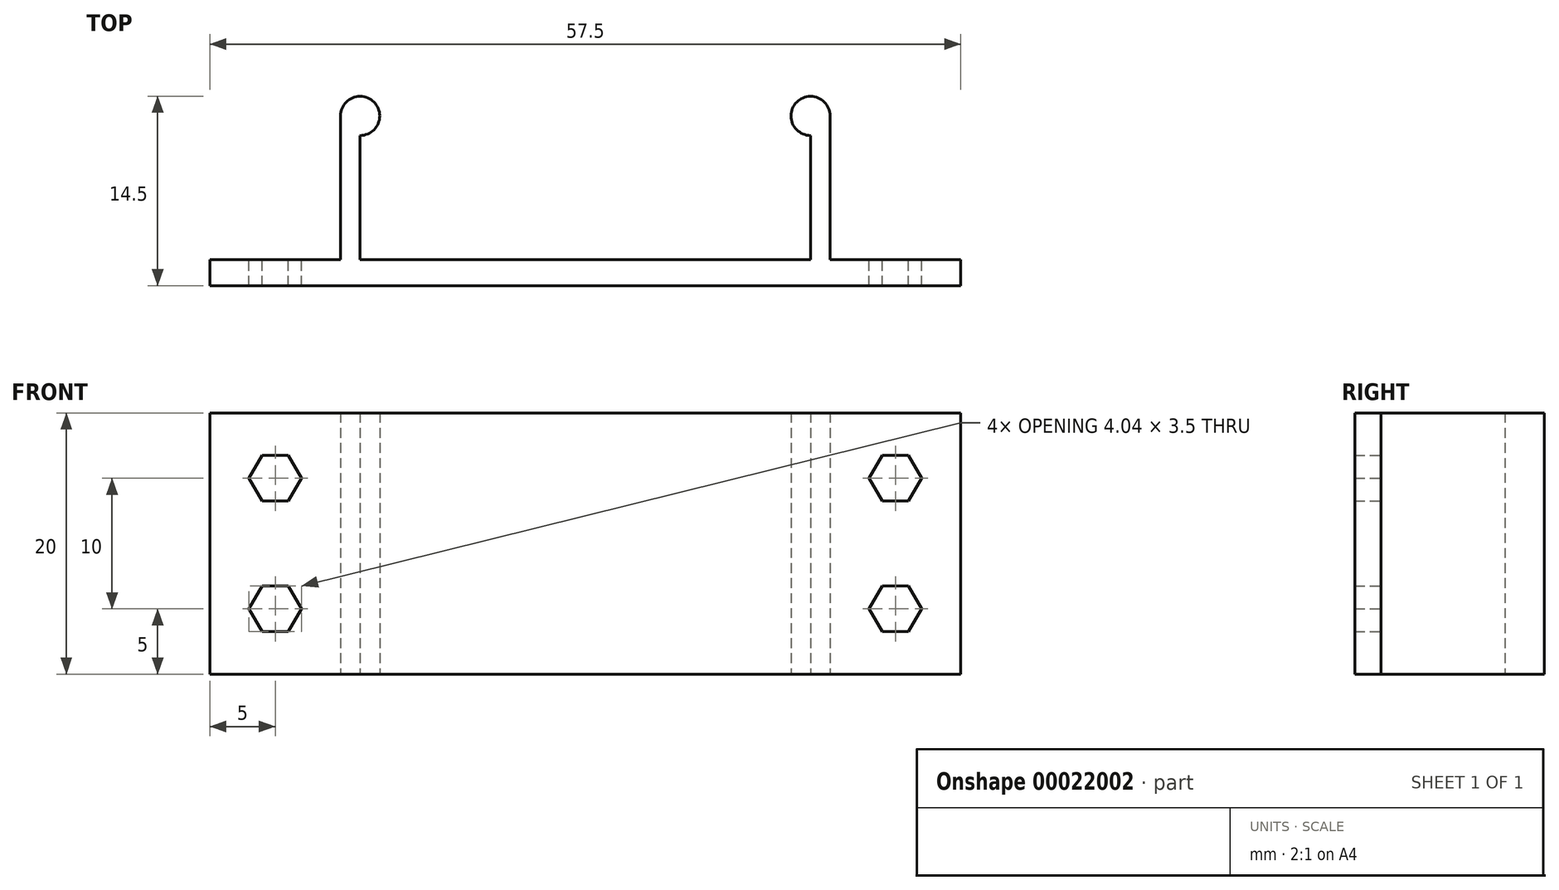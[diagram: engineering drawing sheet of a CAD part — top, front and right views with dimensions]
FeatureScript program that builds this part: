
annotation { "Feature Type Name" : "Feature", "Feature Type Description" : "" }
export const myFeature = defineFeature(function(context is Context, id is Id, definition is map)
    precondition{}
    {
        {
            var Q0;
            Q0=qCreatedBy(makeId("Top.planeOp"),FACE);
            var sketch = newSketch(context, id + "F0", { "sketchPlane" : qUnion([Q0])});
            skLineSegment(sketch, "E0.rect.bottom", {"start": v(17.25, -5.5) * mm, "end": v(-17.25, -5.5) * mm, "construction": true});
            skLineSegment(sketch, "E0.rect.top", {"start": v(17.25, 5.5) * mm, "end": v(-17.25, 5.5) * mm, "construction": true});
            skLineSegment(sketch, "E0.rect.left", {"start": v(17.25, -5.5) * mm, "end": v(17.25, 5.5) * mm, "construction": true});
            skLineSegment(sketch, "E0.rect.right", {"start": v(-17.25, -5.5) * mm, "end": v(-17.25, 5.5) * mm, "construction": true});
            skPoint(sketch, "E0.rect.middle", {"position": v(0, 0) * mm});
            skLineSegment(sketch, "E1", {"start": v(-17.25, 4) * mm, "end": v(-17.25, -5.5) * mm});
            skLineSegment(sketch, "E2", {"start": v(-17.25, -5.5) * mm, "end": v(17.25, -5.5) * mm});
            skLineSegment(sketch, "E3", {"start": v(17.25, -5.5) * mm, "end": v(17.25, 4) * mm});
            skLineSegment(sketch, "E4", {"start": v(-17.25, 5.5) * mm, "end": v(-18.75, 5.5) * mm, "construction": true});
            skLineSegment(sketch, "E5", {"start": v(-18.75, 5.5) * mm, "end": v(-18.75, -5.5) * mm});
            skLineSegment(sketch, "E6", {"start": v(-18.75, -5.5) * mm, "end": v(-28.75, -5.5) * mm});
            skLineSegment(sketch, "E7", {"start": v(-28.75, -5.5) * mm, "end": v(-28.75, -7.5) * mm});
            skLineSegment(sketch, "E8", {"start": v(-28.75, -7.5) * mm, "end": v(28.75, -7.5) * mm});
            skLineSegment(sketch, "E9", {"start": v(28.75, -7.5) * mm, "end": v(28.75, -5.5) * mm});
            skLineSegment(sketch, "E10", {"start": v(28.75, -5.5) * mm, "end": v(18.75, -5.5) * mm});
            skLineSegment(sketch, "E11", {"start": v(18.75, -5.5) * mm, "end": v(18.75, 5.5) * mm});
            skLineSegment(sketch, "E12", {"start": v(18.75, 5.5) * mm, "end": v(17.25, 5.5) * mm, "construction": true});
            skArc(sketch, "E13", {"start": v(-17.25, 4) * mm, "mid": v(-16.19, 6.56) * mm, "end": v(-18.75, 5.5) * mm});
            skArc(sketch, "E14", {"start": v(18.75, 5.5) * mm, "mid": v(16.19, 6.56) * mm, "end": v(17.25, 4) * mm});
            skSolve(sketch);
        }
        {
            var Q0;
            Q0 = qSketchRegion(id + "F0", true);
            extrude(context, id + "F1", {"entities" : qUnion([Q0]), "depth" : 20 * mm});
        }
        {
            var Q0;
            Q0=qCreatedBy(makeId("Front.planeOp"),FACE);
            var sketch = newSketch(context, id + "F2", { "sketchPlane" : qUnion([Q0])});
            skCircle(sketch, "E15.cCircle", {"center": v(23.75, 15) * mm, "radius": 1.75 * mm, "construction": true});
            skLineSegment(sketch, "E15.0", {"start": v(22.74, 13.25) * mm, "end": v(21.73, 15) * mm});
            skLineSegment(sketch, "E15.1", {"start": v(21.73, 15) * mm, "end": v(22.74, 16.75) * mm});
            skLineSegment(sketch, "E15.2", {"start": v(22.74, 16.75) * mm, "end": v(24.76, 16.75) * mm});
            skLineSegment(sketch, "E15.3", {"start": v(24.76, 16.75) * mm, "end": v(25.77, 15) * mm});
            skLineSegment(sketch, "E15.4", {"start": v(25.77, 15) * mm, "end": v(24.76, 13.25) * mm});
            skLineSegment(sketch, "E15.5", {"start": v(24.76, 13.25) * mm, "end": v(22.74, 13.25) * mm});
            skPoint(sketch, "E15.0.midPoint", {"position": v(22.23, 14.13) * mm});
            skCircle(sketch, "E16.cCircle", {"center": v(23.75, 5) * mm, "radius": 1.75 * mm, "construction": true});
            skLineSegment(sketch, "E16.0", {"start": v(22.74, 3.25) * mm, "end": v(21.73, 5) * mm});
            skLineSegment(sketch, "E16.1", {"start": v(21.73, 5) * mm, "end": v(22.74, 6.75) * mm});
            skLineSegment(sketch, "E16.2", {"start": v(22.74, 6.75) * mm, "end": v(24.76, 6.75) * mm});
            skLineSegment(sketch, "E16.3", {"start": v(24.76, 6.75) * mm, "end": v(25.77, 5) * mm});
            skLineSegment(sketch, "E16.4", {"start": v(25.77, 5) * mm, "end": v(24.76, 3.25) * mm});
            skLineSegment(sketch, "E16.5", {"start": v(24.76, 3.25) * mm, "end": v(22.74, 3.25) * mm});
            skPoint(sketch, "E16.0.midPoint", {"position": v(22.23, 4.13) * mm});
            skCircle(sketch, "E17.cCircle", {"center": v(-23.75, 15) * mm, "radius": 1.75 * mm, "construction": true});
            skLineSegment(sketch, "E17.0", {"start": v(-24.76, 13.25) * mm, "end": v(-25.77, 15) * mm});
            skLineSegment(sketch, "E17.1", {"start": v(-25.77, 15) * mm, "end": v(-24.76, 16.75) * mm});
            skLineSegment(sketch, "E17.2", {"start": v(-24.76, 16.75) * mm, "end": v(-22.74, 16.75) * mm});
            skLineSegment(sketch, "E17.3", {"start": v(-22.74, 16.75) * mm, "end": v(-21.73, 15) * mm});
            skLineSegment(sketch, "E17.4", {"start": v(-21.73, 15) * mm, "end": v(-22.74, 13.25) * mm});
            skLineSegment(sketch, "E17.5", {"start": v(-22.74, 13.25) * mm, "end": v(-24.76, 13.25) * mm});
            skPoint(sketch, "E17.0.midPoint", {"position": v(-25.27, 14.13) * mm});
            skCircle(sketch, "E18.cCircle", {"center": v(-23.75, 5) * mm, "radius": 1.75 * mm, "construction": true});
            skLineSegment(sketch, "E18.0", {"start": v(-24.76, 3.25) * mm, "end": v(-25.77, 5) * mm});
            skLineSegment(sketch, "E18.1", {"start": v(-25.77, 5) * mm, "end": v(-24.76, 6.75) * mm});
            skLineSegment(sketch, "E18.2", {"start": v(-24.76, 6.75) * mm, "end": v(-22.74, 6.75) * mm});
            skLineSegment(sketch, "E18.3", {"start": v(-22.74, 6.75) * mm, "end": v(-21.73, 5) * mm});
            skLineSegment(sketch, "E18.4", {"start": v(-21.73, 5) * mm, "end": v(-22.74, 3.25) * mm});
            skLineSegment(sketch, "E18.5", {"start": v(-22.74, 3.25) * mm, "end": v(-24.76, 3.25) * mm});
            skPoint(sketch, "E18.0.midPoint", {"position": v(-25.27, 4.13) * mm});
            skLineSegment(sketch, "E19.0", {"start": v(23.75, 15) * mm, "end": v(23.75, 5) * mm, "construction": true});
            skLineSegment(sketch, "E19.1", {"start": v(-23.75, 15) * mm, "end": v(23.75, 15) * mm, "construction": true});
            skLineSegment(sketch, "E19.2", {"start": v(-23.75, 15) * mm, "end": v(-23.75, 5) * mm, "construction": true});
            skLineSegment(sketch, "E19.3", {"start": v(-23.75, 5) * mm, "end": v(23.75, 5) * mm, "construction": true});
            skSolve(sketch);
        }
        {
            var Q0;
            Q0 = qSketchRegion(id + "F2", true);
            extrude(context, id + "F3", {"entities" : qUnion([Q0]), "operationType" : NewBodyOperationType.REMOVE, "depth" : 25 * mm});
        }
    });
